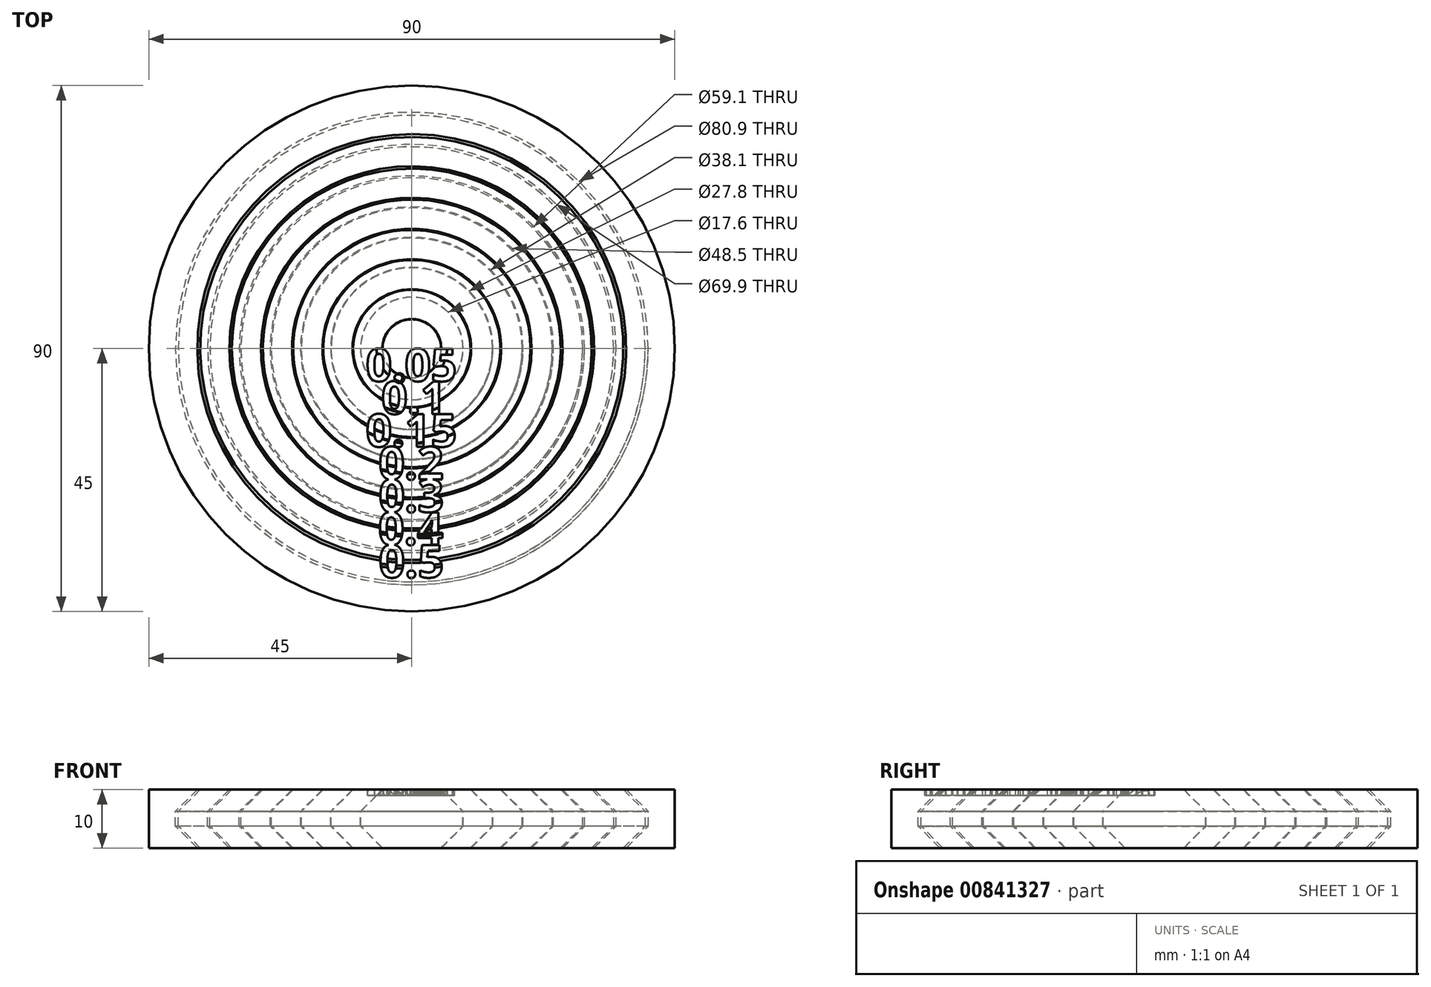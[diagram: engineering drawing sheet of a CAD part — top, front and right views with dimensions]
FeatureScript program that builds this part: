
annotation { "Feature Type Name" : "Feature", "Feature Type Description" : "" }
export const myFeature = defineFeature(function(context is Context, id is Id, definition is map)
    precondition{}
    {
        {
            var Q0;
            Q0=qCreatedBy(makeId("Top.planeOp"),FACE);
            var sketch = newSketch(context, id + "F0", { "sketchPlane" : qUnion([Q0])});
            skCircle(sketch, "E0", {"center": v(0, 0) * mm, "radius": 45 * mm});
            skSolve(sketch);
        }
        {
            var Q0;
            Q0 = qSketchRegion(id + "F0", true);
            extrude(context, id + "F1", {"entities" : qUnion([Q0]), "endBound" : BoundingType.SYMMETRIC, "depth" : 10 * mm, "offsetDistance" : 25 * mm});
        }
        {
            var Q0;
            Q0=qCreatedBy(makeId("Front.planeOp"),FACE);
            var sketch = newSketch(context, id + "F2", { "sketchPlane" : qUnion([Q0])});
            skLineSegment(sketch, "E1", {"start": v(5, 5) * mm, "end": v(5.05, 5) * mm});
            skLineSegment(sketch, "E2", {"start": v(5.05, 5) * mm, "end": v(8.8, 1.25) * mm});
            skLineSegment(sketch, "E3", {"start": v(8.8, 1.25) * mm, "end": v(8.8, -1.25) * mm});
            skLineSegment(sketch, "E4", {"start": v(8.8, -1.25) * mm, "end": v(5.05, -5) * mm});
            skLineSegment(sketch, "E5", {"start": v(5.05, -5) * mm, "end": v(5, -5) * mm});
            skLineSegment(sketch, "E6", {"start": v(5, -5) * mm, "end": v(8.75, -1.25) * mm});
            skLineSegment(sketch, "E7", {"start": v(8.75, -1.25) * mm, "end": v(8.75, 1.25) * mm});
            skLineSegment(sketch, "E8", {"start": v(8.75, 1.25) * mm, "end": v(5, 5) * mm});
            skLineSegment(sketch, "E9", {"start": v(10.05, 5) * mm, "end": v(10.15, 5) * mm});
            skLineSegment(sketch, "E10", {"start": v(10.15, 5) * mm, "end": v(13.9, 1.25) * mm});
            skLineSegment(sketch, "E11", {"start": v(13.9, 1.25) * mm, "end": v(13.9, -1.25) * mm});
            skLineSegment(sketch, "E12", {"start": v(13.9, -1.25) * mm, "end": v(10.15, -5) * mm});
            skLineSegment(sketch, "E13", {"start": v(10.15, -5) * mm, "end": v(10.05, -5) * mm});
            skLineSegment(sketch, "E14", {"start": v(10.05, -5) * mm, "end": v(13.8, -1.25) * mm});
            skLineSegment(sketch, "E15", {"start": v(13.8, -1.25) * mm, "end": v(13.8, 1.25) * mm});
            skLineSegment(sketch, "E16", {"start": v(13.8, 1.25) * mm, "end": v(10.05, 5) * mm});
            skLineSegment(sketch, "E17", {"start": v(15.15, 5) * mm, "end": v(15.3, 5) * mm});
            skLineSegment(sketch, "E18", {"start": v(15.3, 5) * mm, "end": v(19.05, 1.25) * mm});
            skLineSegment(sketch, "E19", {"start": v(19.05, 1.25) * mm, "end": v(19.05, -1.25) * mm});
            skLineSegment(sketch, "E20", {"start": v(19.05, -1.25) * mm, "end": v(15.3, -5) * mm});
            skLineSegment(sketch, "E21", {"start": v(15.3, -5) * mm, "end": v(15.15, -5) * mm});
            skLineSegment(sketch, "E22", {"start": v(15.15, -5) * mm, "end": v(18.9, -1.25) * mm});
            skLineSegment(sketch, "E23", {"start": v(18.9, -1.25) * mm, "end": v(18.9, 1.25) * mm});
            skLineSegment(sketch, "E24", {"start": v(18.9, 1.25) * mm, "end": v(15.15, 5) * mm});
            skLineSegment(sketch, "E25", {"start": v(20.3, 5) * mm, "end": v(20.5, 5) * mm});
            skLineSegment(sketch, "E26", {"start": v(20.5, 5) * mm, "end": v(24.25, 1.25) * mm});
            skLineSegment(sketch, "E27", {"start": v(24.25, 1.25) * mm, "end": v(24.25, -1.25) * mm});
            skLineSegment(sketch, "E28", {"start": v(24.25, -1.25) * mm, "end": v(20.5, -5) * mm});
            skLineSegment(sketch, "E29", {"start": v(20.5, -5) * mm, "end": v(20.3, -5) * mm});
            skLineSegment(sketch, "E30", {"start": v(20.3, -5) * mm, "end": v(24.05, -1.25) * mm});
            skLineSegment(sketch, "E31", {"start": v(24.05, -1.25) * mm, "end": v(24.05, 1.25) * mm});
            skLineSegment(sketch, "E32", {"start": v(24.05, 1.25) * mm, "end": v(20.3, 5) * mm});
            skLineSegment(sketch, "E33", {"start": v(25.5, 5) * mm, "end": v(25.8, 5) * mm});
            skLineSegment(sketch, "E34", {"start": v(25.8, 5) * mm, "end": v(29.55, 1.25) * mm});
            skLineSegment(sketch, "E35", {"start": v(29.55, 1.25) * mm, "end": v(29.55, -1.25) * mm});
            skLineSegment(sketch, "E36", {"start": v(29.55, -1.25) * mm, "end": v(25.8, -5) * mm});
            skLineSegment(sketch, "E37", {"start": v(25.8, -5) * mm, "end": v(25.5, -5) * mm});
            skLineSegment(sketch, "E38", {"start": v(25.5, -5) * mm, "end": v(29.25, -1.25) * mm});
            skLineSegment(sketch, "E39", {"start": v(29.25, -1.25) * mm, "end": v(29.25, 1.25) * mm});
            skLineSegment(sketch, "E40", {"start": v(29.25, 1.25) * mm, "end": v(25.5, 5) * mm});
            skLineSegment(sketch, "E41", {"start": v(30.8, 5) * mm, "end": v(31.2, 5) * mm});
            skLineSegment(sketch, "E42", {"start": v(31.2, 5) * mm, "end": v(34.95, 1.25) * mm});
            skLineSegment(sketch, "E43", {"start": v(34.95, 1.25) * mm, "end": v(34.95, -1.25) * mm});
            skLineSegment(sketch, "E44", {"start": v(34.95, -1.25) * mm, "end": v(31.2, -5) * mm});
            skLineSegment(sketch, "E45", {"start": v(31.2, -5) * mm, "end": v(30.8, -5) * mm});
            skLineSegment(sketch, "E46", {"start": v(30.8, -5) * mm, "end": v(34.55, -1.25) * mm});
            skLineSegment(sketch, "E47", {"start": v(34.55, -1.25) * mm, "end": v(34.55, 1.25) * mm});
            skLineSegment(sketch, "E48", {"start": v(34.55, 1.25) * mm, "end": v(30.8, 5) * mm});
            skLineSegment(sketch, "E49", {"start": v(36.2, 5) * mm, "end": v(36.7, 5) * mm});
            skLineSegment(sketch, "E50", {"start": v(36.7, 5) * mm, "end": v(40.45, 1.25) * mm});
            skLineSegment(sketch, "E51", {"start": v(40.45, 1.25) * mm, "end": v(40.45, -1.25) * mm});
            skLineSegment(sketch, "E52", {"start": v(40.45, -1.25) * mm, "end": v(36.7, -5) * mm});
            skLineSegment(sketch, "E53", {"start": v(36.7, -5) * mm, "end": v(36.2, -5) * mm});
            skLineSegment(sketch, "E54", {"start": v(36.2, -5) * mm, "end": v(39.95, -1.25) * mm});
            skLineSegment(sketch, "E55", {"start": v(39.95, -1.25) * mm, "end": v(39.95, 1.25) * mm});
            skLineSegment(sketch, "E56", {"start": v(39.95, 1.25) * mm, "end": v(36.2, 5) * mm});
            skLineSegment(sketch, "E57", {"start": v(0, 0) * mm, "end": v(0, 10.92) * mm, "construction": true});
            skSolve(sketch);
        }
        {
            var Q0;
            Q0 = qSketchRegion(id + "F2", true);
            var Q1;
            Q1=sQuery(id+"F2.wireOp",EDGE,"E57");
            revolve(context, id + "F3", {"operationType" : NewBodyOperationType.REMOVE, "surfaceOperationType" : NewSurfaceOperationType.NEW, "entities" : qUnion([Q0]), "axis" : qUnion([Q1]), "revolveType" : RevolveType.FULL, "oppositeDirection" : true});
        }
        {
            var Q0;
            {var subQ0=sQuery(id+"F0.wireOp",EDGE,"E0");Q0=makeQuery(id+"F3.boolean.opBoolean","SPLIT",FACE,{"disambiguationData":[TD([makeQuery(id+"F1.opExtrude","SWEPT_FACE",FACE,{"disambiguationData":[OSD([subQ0])]})])],"derivedFrom":makeQuery(id+"F1.opExtrude","CAP_FACE",FACE,{"disambiguationData":[OSD([subQ0])],"isStart":false})});}
            var sketch = newSketch(context, id + "F4", { "sketchPlane" : qUnion([Q0])});
            skText(sketch, "E58", { "text": "0.05", "fontName": "OpenSans-Bold.ttf"});
            skLineSegment(sketch, "E59", {"start": v(0, 0) * mm, "end": v(0, -59.42) * mm, "construction": true});
            skText(sketch, "E60", { "text": "0.1", "fontName": "OpenSans-Bold.ttf"});
            skText(sketch, "E61", { "text": "0.15", "fontName": "OpenSans-Bold.ttf"});
            skText(sketch, "E62", { "text": "0.2", "fontName": "OpenSans-Bold.ttf"});
            skText(sketch, "E63", { "text": "0.3", "fontName": "OpenSans-Bold.ttf"});
            skText(sketch, "E64", { "text": "0.4", "fontName": "OpenSans-Bold.ttf"});
            skText(sketch, "E65", { "text": "0.5", "fontName": "OpenSans-Bold.ttf"});
            const initialGuessF4  = {"E58": [-0.00785, -0.0056, 1, 0, 0.0056], "E60": [-0.00519, -0.0112, 1, 0, 0.0056], "E61": [-0.00785, -0.0168, 1, 0, 0.0056], "E62": [-0.00568, -0.0224, 1, 0, 0.0056], "E63": [-0.00565, -0.028, 1, 0, 0.0056], "E64": [-0.00574, -0.0336, 1, 0, 0.0056], "E65": [-0.00563, -0.0392, 1, 0, 0.0056]};
            skSetInitialGuess(sketch, initialGuessF4);
            skSolve(sketch);
        }
        {
            var Q0;
            Q0 = qSketchRegion(id + "F4", true);
            extrude(context, id + "F5", {"entities" : qUnion([Q0]), "operationType" : NewBodyOperationType.REMOVE, "oppositeDirection" : true, "depth" : 1 * mm, "offsetDistance" : 25 * mm});
        }
    });
